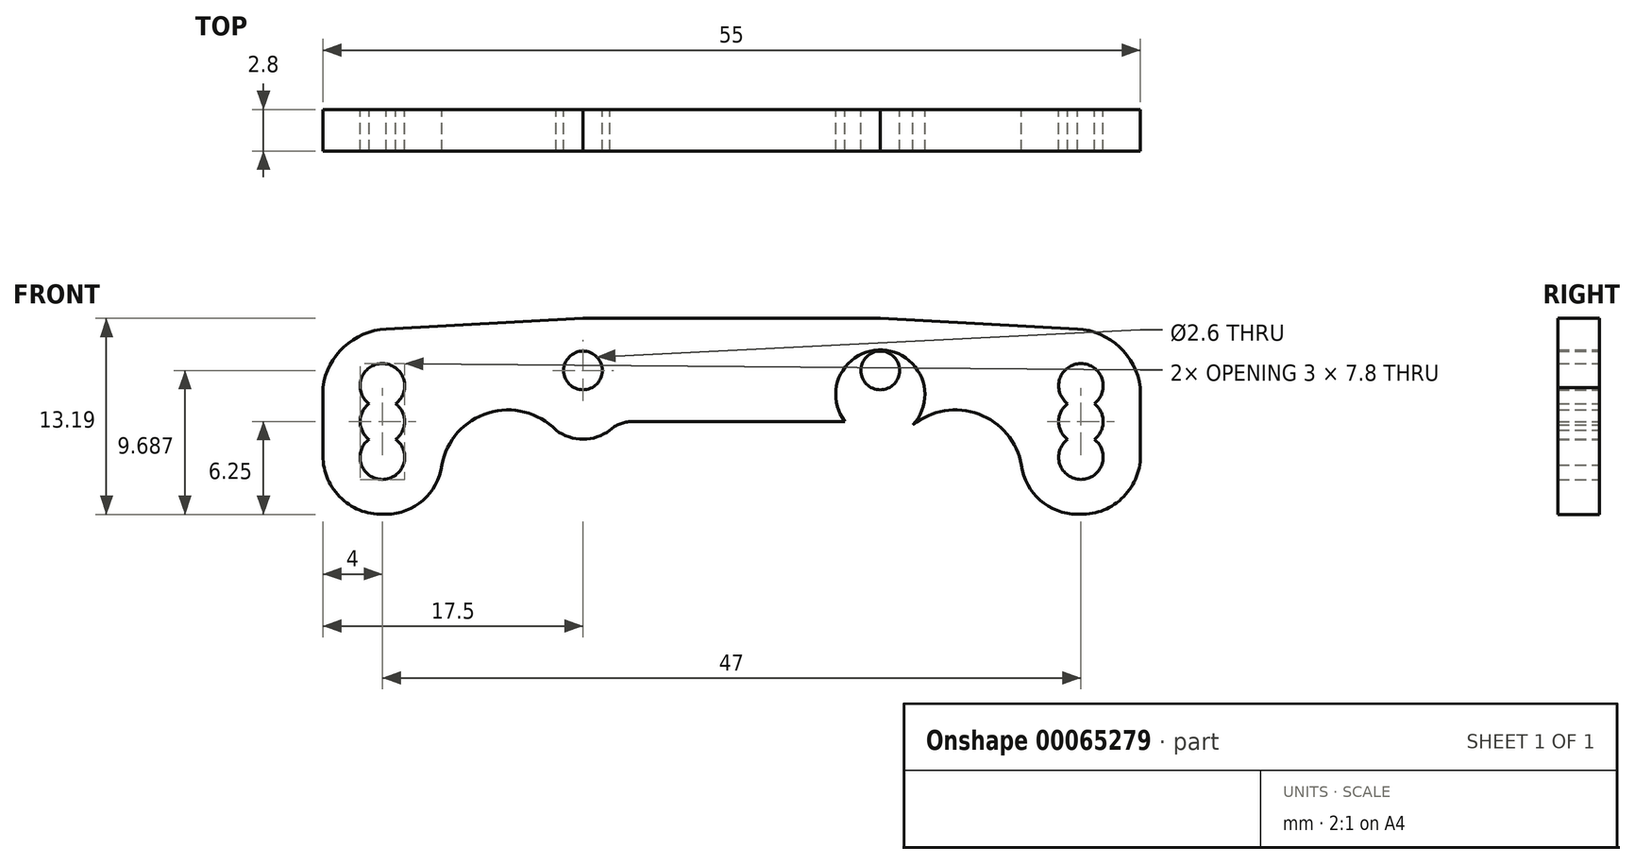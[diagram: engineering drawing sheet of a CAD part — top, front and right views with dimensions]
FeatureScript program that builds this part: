
annotation { "Feature Type Name" : "Feature", "Feature Type Description" : "" }
export const myFeature = defineFeature(function(context is Context, id is Id, definition is map)
    precondition{}
    {
        {
            var Q0;
            Q0=qCreatedBy(makeId("Front.planeOp"),FACE);
            var sketch = newSketch(context, id + "F0", { "sketchPlane" : qUnion([Q0])});
            skLineSegment(sketch, "E0", {"start": v(-27.5, -3.93) * mm, "end": v(-27.5, -8.52) * mm});
            skPoint(sketch, "E1.visualSharp", {"position": v(-27.5, -12.45) * mm});
            skArc(sketch, "E1.filletArc", {"start": v(-27.5, -8.52) * mm, "mid": v(-26.24, -11.41) * mm, "end": v(-23.26, -12.45) * mm});
            skLineSegment(sketch, "E2", {"start": v(-23.26, 0) * mm, "end": v(-10, 0.72) * mm});
            skLineSegment(sketch, "E3", {"start": v(-23.26, -12.45) * mm, "end": v(-23.26, -12.45) * mm});
            skPoint(sketch, "E4.visualSharp", {"position": v(-19.31, -12.45) * mm});
            skPoint(sketch, "E5.visualSharp", {"position": v(-19.61, -7) * mm});
            skLineSegment(sketch, "E6", {"start": v(-10, 0.72) * mm, "end": v(0.03, 0.72) * mm});
            skArc(sketch, "E7", {"start": v(-23.26, 0) * mm, "mid": v(-26.09, -1.2) * mm, "end": v(-27.5, -3.93) * mm});
            skCircle(sketch, "E8", {"center": v(-10, -2.78) * mm, "radius": 1.3 * mm});
            skCircle(sketch, "E9", {"center": v(-10, -4.4) * mm, "radius": 3 * mm});
            skArc(sketch, "E10", {"start": v(-23.26, -12.45) * mm, "mid": v(-20.76, -11.51) * mm, "end": v(-19.5, -9.16) * mm});
            skLineSegment(sketch, "E11", {"start": v(-16.95, -7.43) * mm, "end": v(-16.95, -7.3) * mm});
            skArc(sketch, "E12", {"start": v(-11.81, -6.8) * mm, "mid": v(-16.38, -5.64) * mm, "end": v(-19.5, -9.16) * mm});
            skLineSegment(sketch, "E13", {"start": v(0, -6.23) * mm, "end": v(-7.61, -6.23) * mm});
            skArc(sketch, "E14", {"start": v(-6.72, -6.23) * mm, "mid": v(-7.5, -6.37) * mm, "end": v(-8.19, -6.8) * mm});
            skCircle(sketch, "E15", {"center": v(-23.5, -3.82) * mm, "radius": 1.5 * mm});
            skCircle(sketch, "E16", {"center": v(-23.5, -6.22) * mm, "radius": 1.5 * mm});
            skCircle(sketch, "E17", {"center": v(-23.5, -8.62) * mm, "radius": 1.5 * mm});
            skPoint(sketch, "E18.MirrorP", {"position": v(19.61, -7) * mm});
            skCircle(sketch, "E19.MirrorC", {"center": v(23.5, -6.22) * mm, "radius": 1.5 * mm});
            skCircle(sketch, "E20.MirrorC", {"center": v(23.5, -8.62) * mm, "radius": 1.5 * mm});
            skLineSegment(sketch, "E21.MirrorCS", {"start": v(27.5, -3.93) * mm, "end": v(27.5, -8.52) * mm});
            skArc(sketch, "E22.MirrorCS", {"start": v(6.72, -6.23) * mm, "mid": v(7.5, -6.37) * mm, "end": v(8.19, -6.8) * mm});
            skCircle(sketch, "E23.MirrorC", {"center": v(23.5, -3.82) * mm, "radius": 1.5 * mm});
            skArc(sketch, "E24.MirrorCS", {"start": v(27.5, -8.52) * mm, "mid": v(26.24, -11.41) * mm, "end": v(23.26, -12.45) * mm});
            skLineSegment(sketch, "E25.MirrorCS", {"start": v(23.26, 0) * mm, "end": v(10, 0.72) * mm});
            skArc(sketch, "E26.MirrorCS", {"start": v(23.26, 0) * mm, "mid": v(26.09, -1.2) * mm, "end": v(27.5, -3.93) * mm});
            skPoint(sketch, "E27.MirrorP", {"position": v(27.5, -12.45) * mm});
            skLineSegment(sketch, "E28.MirrorCS", {"start": v(0, -6.23) * mm, "end": v(7.61, -6.23) * mm});
            skLineSegment(sketch, "E29.MirrorCS", {"start": v(10, 0.72) * mm, "end": v(-0.03, 0.72) * mm});
            skCircle(sketch, "E30.MirrorC", {"center": v(10, -2.78) * mm, "radius": 1.3 * mm});
            skCircle(sketch, "E31.MirrorC", {"center": v(10, -4.4) * mm, "radius": 3 * mm});
            skArc(sketch, "E32.MirrorCS", {"start": v(23.26, -12.45) * mm, "mid": v(20.76, -11.51) * mm, "end": v(19.5, -9.16) * mm});
            skArc(sketch, "E33.MirrorCS", {"start": v(11.81, -6.8) * mm, "mid": v(16.38, -5.64) * mm, "end": v(19.5, -9.16) * mm});
            skPoint(sketch, "E34.MirrorP", {"position": v(19.31, -12.45) * mm});
            skSolve(sketch);
        }
        {
            var Q0;
            Q0=makeQuery(id+"F0.imprint","IMPRINT",FACE,{"disambiguationData":[TD([[makeQuery(id+"F0.imprint","IMPRINT",EDGE,{"derivedFrom":sQuery(id+"F0.wireOp",EDGE,"E0")}),1.0]])]});
            var Q1;
            {var subQ0=sQuery(id+"F0.wireOp",EDGE,"3175dec5-ecc8-497a-94e0-c18c9048b3d79.MirrorC");var subQ1=sQuery(id+"F0.wireOp",EDGE,"3175dec5-ecc8-497a-94e0-c18c9048b3d78.MirrorC");var subQ2=makeQuery(id+"F0.imprint","INTERSECT",VERTEX,{"disambiguationData":[OD(0.0)],"derivedFrom":[subQ1,subQ0]});Q1=makeQuery(id+"F0.imprint","IMPRINT",FACE,{"disambiguationData":[TD([[makeQuery(id+"F0.imprint","IMPRINT",EDGE,{"disambiguationData":[TD([[subQ2,-1.0]])],"derivedFrom":subQ1}),1.0]])]});}
            var Q2;
            {var subQ0=sQuery(id+"F0.wireOp",EDGE,"E9");var subQ1=sQuery(id+"F0.wireOp",EDGE,"E8");var subQ2=makeQuery(id+"F0.imprint","INTERSECT",VERTEX,{"disambiguationData":[OD(0.0)],"derivedFrom":[subQ1,subQ0]});Q2=makeQuery(id+"F0.imprint","IMPRINT",FACE,{"disambiguationData":[TD([[makeQuery(id+"F0.imprint","IMPRINT",EDGE,{"disambiguationData":[TD([[subQ2,-1.0]])],"derivedFrom":subQ1}),-1.0]])]});}
            var Q3;
            {var subQ0=sQuery(id+"F0.wireOp",EDGE,"4947ccc5-f163-4911-af9b-3670b5c434d87.MirrorC");var subQ1=sQuery(id+"F0.wireOp",EDGE,"4947ccc5-f163-4911-af9b-3670b5c434d81.MirrorC");var subQ2=makeQuery(id+"F0.imprint","INTERSECT",VERTEX,{"disambiguationData":[OD(0.0)],"derivedFrom":[subQ1,subQ0]});Q3=makeQuery(id+"F0.imprint","IMPRINT",FACE,{"disambiguationData":[TD([[makeQuery(id+"F0.imprint","IMPRINT",EDGE,{"disambiguationData":[TD([[subQ2,-1.0]])],"derivedFrom":subQ1}),1.0]])]});}
            var Q4;
            Q4=makeQuery(id+"F0.imprint","IMPRINT",FACE,{"disambiguationData":[TD([[makeQuery(id+"F0.imprint","IMPRINT",EDGE,{"derivedFrom":sQuery(id+"F0.wireOp",EDGE,"f9352994-d9aa-4b82-b3cd-584cf7b527e77.MirrorC")}),1.0]])]});
            var Q5;
            {var subQ0=sQuery(id+"F0.wireOp",EDGE,"E13");var subQ1=sQuery(id+"F0.wireOp",EDGE,"E9");var subQ2=makeQuery(id+"F0.imprint","INTERSECT",VERTEX,{"derivedFrom":[subQ1,subQ0]});Q5=makeQuery(id+"F0.imprint","IMPRINT",FACE,{"disambiguationData":[TD([[makeQuery(id+"F0.imprint","IMPRINT",EDGE,{"disambiguationData":[TD([[subQ2,1.0]])],"derivedFrom":subQ1}),-1.0]])]});}
            var Q6;
            Q6=makeQuery(id+"F0.imprint","IMPRINT",FACE,{"disambiguationData":[TD([[makeQuery(id+"F0.imprint","IMPRINT",EDGE,{"derivedFrom":sQuery(id+"F0.wireOp",EDGE,"adcd29ed-2caf-40d0-b99b-ca4b536d659412.MirrorC")}),1.0]])]});
            var Q7;
            {var subQ0=sQuery(id+"F0.wireOp",EDGE,"adcd29ed-2caf-40d0-b99b-ca4b536d65941.MirrorCS");var subQ1=sQuery(id+"F0.wireOp",EDGE,"adcd29ed-2caf-40d0-b99b-ca4b536d65940.MirrorCS");var subQ2=makeQuery(id+"F0.imprint","INTERSECT",VERTEX,{"disambiguationData":[OD(1.0)],"derivedFrom":[subQ1,subQ0]});Q7=makeQuery(id+"F0.imprint","IMPRINT",FACE,{"disambiguationData":[TD([[makeQuery(id+"F0.imprint","IMPRINT",EDGE,{"disambiguationData":[TD([[subQ2,-1.0]])],"derivedFrom":subQ1}),1.0]])]});}
            var Q8;
            Q8=makeQuery(id+"F0.imprint","IMPRINT",FACE,{"disambiguationData":[TD([[makeQuery(id+"F0.imprint","IMPRINT",EDGE,{"derivedFrom":sQuery(id+"F0.wireOp",EDGE,"E30.MirrorC")}),1.0]])]});
            var Q9;
            {var subQ0=sQuery(id+"F0.wireOp",EDGE,"E28.MirrorCS");var subQ1=sQuery(id+"F0.wireOp",EDGE,"E22.MirrorCS");var subQ2=makeQuery(id+"F0.imprint","INTERSECT",VERTEX,{"disambiguationData":[OD(1.0)],"derivedFrom":[subQ1,subQ0]});Q9=makeQuery(id+"F0.imprint","IMPRINT",FACE,{"disambiguationData":[TD([[makeQuery(id+"F0.imprint","IMPRINT",EDGE,{"disambiguationData":[TD([[subQ2,-1.0]])],"derivedFrom":subQ1}),1.0]])]});}
            extrude(context, id + "F1", {"entities" : qUnion([Q0, Q1, Q2, Q3, Q4, Q5, Q6, Q7, Q8, Q9]), "depth" : 2.8 * mm});
        }
    });
